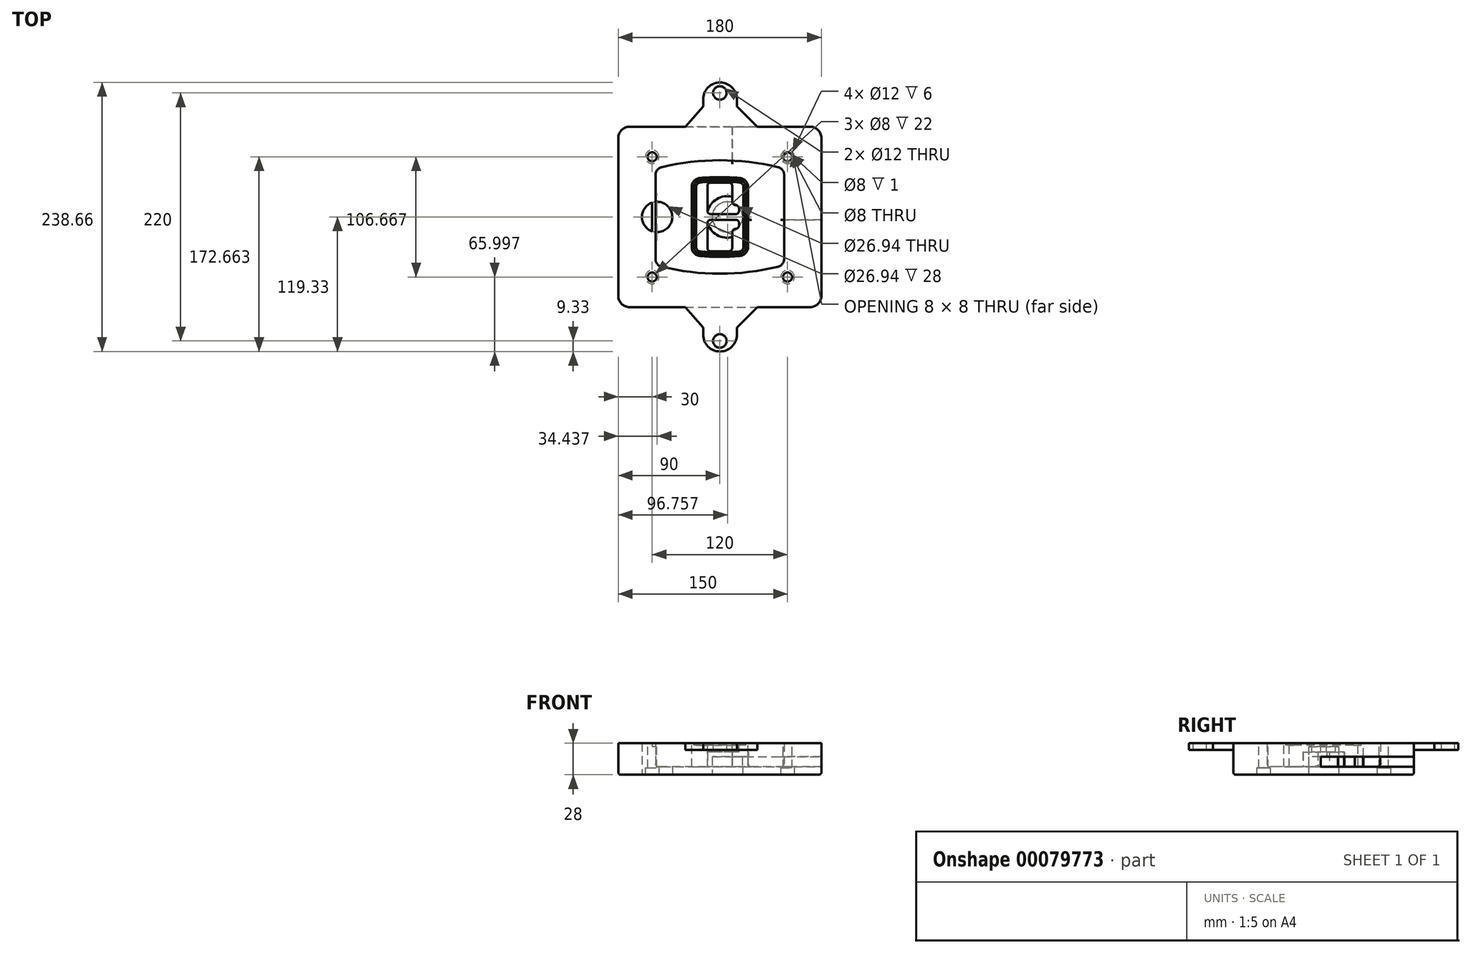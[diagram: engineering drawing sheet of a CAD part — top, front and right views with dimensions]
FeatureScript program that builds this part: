
annotation { "Feature Type Name" : "Feature", "Feature Type Description" : "" }
export const myFeature = defineFeature(function(context is Context, id is Id, definition is map)
    precondition{}
    {
        {
            var Q0;
            Q0=qCreatedBy(makeId("Top.planeOp"),FACE);
            var sketch = newSketch(context, id + "F0", { "sketchPlane" : qUnion([Q0])});
            skPoint(sketch, "E0.rect.middle", {"position": v(0, 0) * mm});
            skLineSegment(sketch, "E1.bottom", {"start": v(-80, -80) * mm, "end": v(80, -80) * mm});
            skLineSegment(sketch, "E1.top", {"start": v(-80, 80) * mm, "end": v(80, 80) * mm});
            skLineSegment(sketch, "E1.left", {"start": v(-90, -70) * mm, "end": v(-90, 70) * mm});
            skLineSegment(sketch, "E1.right", {"start": v(90, -70) * mm, "end": v(90, 70) * mm});
            skLineSegment(sketch, "E2", {"start": v(-90, 80) * mm, "end": v(90, -80) * mm, "construction": true});
            skLineSegment(sketch, "E3", {"start": v(90, 80) * mm, "end": v(-90, -80) * mm, "construction": true});
            skCircle(sketch, "E4", {"center": v(-60, 53.33) * mm, "radius": 4 * mm});
            skCircle(sketch, "E5", {"center": v(60, 53.33) * mm, "radius": 4 * mm});
            skCircle(sketch, "E6", {"center": v(60, -53.33) * mm, "radius": 4 * mm});
            skCircle(sketch, "E7", {"center": v(-60, -53.33) * mm, "radius": 4 * mm});
            skLineSegment(sketch, "E8", {"start": v(-60, 53.33) * mm, "end": v(60, 53.33) * mm, "construction": true});
            skLineSegment(sketch, "E9", {"start": v(60, 53.33) * mm, "end": v(60, -53.33) * mm, "construction": true});
            skLineSegment(sketch, "E10", {"start": v(60, -53.33) * mm, "end": v(-60, -53.33) * mm, "construction": true});
            skLineSegment(sketch, "E11", {"start": v(-60, -53.33) * mm, "end": v(-60, 53.33) * mm, "construction": true});
            skLineSegment(sketch, "E12", {"start": v(-60, 37.3) * mm, "end": v(-60, -37.3) * mm});
            skLineSegment(sketch, "E13", {"start": v(60, 37.3) * mm, "end": v(60, -37.3) * mm});
            skArc(sketch, "E14", {"start": v(52.38, 47.01) * mm, "mid": v(0, 53.33) * mm, "end": v(-52.38, 47.01) * mm});
            skArc(sketch, "E15", {"start": v(-52.38, -47.01) * mm, "mid": v(0, -53.33) * mm, "end": v(52.38, -47.01) * mm});
            skLineSegment(sketch, "E16", {"start": v(-60, 0) * mm, "end": v(60, 0) * mm, "construction": true});
            skPoint(sketch, "E17.visualSharp", {"position": v(-60, -45) * mm});
            skArc(sketch, "E17.filletArc", {"start": v(-60, -37.3) * mm, "mid": v(-57.87, -43.47) * mm, "end": v(-52.38, -47.01) * mm});
            skPoint(sketch, "E18.visualSharp", {"position": v(-60, 45) * mm});
            skArc(sketch, "E18.filletArc", {"start": v(-52.38, 47.01) * mm, "mid": v(-57.87, 43.47) * mm, "end": v(-60, 37.3) * mm});
            skPoint(sketch, "E19.visualSharp", {"position": v(60, 45) * mm});
            skArc(sketch, "E19.filletArc", {"start": v(60, 37.3) * mm, "mid": v(57.87, 43.47) * mm, "end": v(52.38, 47.01) * mm});
            skPoint(sketch, "E20.visualSharp", {"position": v(60, -45) * mm});
            skArc(sketch, "E20.filletArc", {"start": v(52.38, -47.01) * mm, "mid": v(57.87, -43.47) * mm, "end": v(60, -37.3) * mm});
            skPoint(sketch, "E21.visualSharp", {"position": v(-90, 80) * mm});
            skArc(sketch, "E21.filletArc", {"start": v(-80, 80) * mm, "mid": v(-87.07, 77.07) * mm, "end": v(-90, 70) * mm});
            skPoint(sketch, "E22.visualSharp", {"position": v(90, 80) * mm});
            skArc(sketch, "E22.filletArc", {"start": v(90, 70) * mm, "mid": v(87.07, 77.07) * mm, "end": v(80, 80) * mm});
            skPoint(sketch, "E23.visualSharp", {"position": v(90, -80) * mm});
            skArc(sketch, "E23.filletArc", {"start": v(80, -80) * mm, "mid": v(87.07, -77.07) * mm, "end": v(90, -70) * mm});
            skPoint(sketch, "E24.visualSharp", {"position": v(-90, -80) * mm});
            skArc(sketch, "E24.filletArc", {"start": v(-90, -70) * mm, "mid": v(-87.07, -77.07) * mm, "end": v(-80, -80) * mm});
            skArc(sketch, "E25.0", {"start": v(57, 37.3) * mm, "mid": v(55.5, 41.62) * mm, "end": v(51.67, 44.1) * mm});
            skLineSegment(sketch, "E25.1", {"start": v(57, 37.3) * mm, "end": v(57, -37.3) * mm});
            skArc(sketch, "E25.2", {"start": v(51.67, -44.1) * mm, "mid": v(55.5, -41.62) * mm, "end": v(57, -37.3) * mm});
            skArc(sketch, "E25.3", {"start": v(-51.67, -44.1) * mm, "mid": v(0, -50.33) * mm, "end": v(51.67, -44.1) * mm});
            skArc(sketch, "E25.4", {"start": v(-57, -37.3) * mm, "mid": v(-55.5, -41.62) * mm, "end": v(-51.67, -44.1) * mm});
            skArc(sketch, "E25.5", {"start": v(51.67, 44.1) * mm, "mid": v(0, 50.33) * mm, "end": v(-51.67, 44.1) * mm});
            skLineSegment(sketch, "E25.6", {"start": v(-57, 37.3) * mm, "end": v(-57, -37.3) * mm});
            skArc(sketch, "E25.7", {"start": v(-51.67, 44.1) * mm, "mid": v(-55.5, 41.62) * mm, "end": v(-57, 37.3) * mm});
            skArc(sketch, "E26.0", {"start": v(-53.33, 50.9) * mm, "mid": v(-61.01, 45.94) * mm, "end": v(-64, 37.3) * mm});
            skArc(sketch, "E26.1", {"start": v(53.33, 50.9) * mm, "mid": v(0, 57.33) * mm, "end": v(-53.33, 50.9) * mm});
            skArc(sketch, "E26.2", {"start": v(64, 37.3) * mm, "mid": v(61.01, 45.94) * mm, "end": v(53.33, 50.9) * mm});
            skLineSegment(sketch, "E26.3", {"start": v(64, 37.3) * mm, "end": v(64, -37.3) * mm});
            skArc(sketch, "E26.4", {"start": v(53.33, -50.9) * mm, "mid": v(61.01, -45.94) * mm, "end": v(64, -37.3) * mm});
            skLineSegment(sketch, "E26.5", {"start": v(-64, 37.3) * mm, "end": v(-64, -37.3) * mm});
            skArc(sketch, "E26.6", {"start": v(-53.33, -50.9) * mm, "mid": v(0, -57.33) * mm, "end": v(53.33, -50.9) * mm});
            skArc(sketch, "E26.7", {"start": v(-64, -37.3) * mm, "mid": v(-61.01, -45.94) * mm, "end": v(-53.33, -50.9) * mm});
            skSolve(sketch);
        }
        {
            var Q0;
            Q0=makeQuery(id+"F0.imprint","IMPRINT",FACE,{"disambiguationData":[TD([[makeQuery(id+"F0.imprint","IMPRINT",EDGE,{"derivedFrom":sQuery(id+"F0.wireOp",EDGE,"E1.bottom")}),1.0]])]});
            var Q1;
            Q1=makeQuery(id+"F0.imprint","IMPRINT",FACE,{"disambiguationData":[TD([[makeQuery(id+"F0.imprint","IMPRINT",EDGE,{"derivedFrom":sQuery(id+"F0.wireOp",EDGE,"E12")}),1.0]])]});
            var Q2;
            Q2=makeQuery(id+"F0.imprint","IMPRINT",FACE,{"disambiguationData":[TD([[makeQuery(id+"F0.imprint","IMPRINT",EDGE,{"derivedFrom":sQuery(id+"F0.wireOp",EDGE,"E25.0")}),1.0]])]});
            var Q3;
            Q3=makeQuery(id+"F0.imprint","IMPRINT",FACE,{"disambiguationData":[TD([[makeQuery(id+"F0.imprint","IMPRINT",EDGE,{"derivedFrom":sQuery(id+"F0.wireOp",EDGE,"E12")}),-1.0]])]});
            extrude(context, id + "F1", {"entities" : qUnion([Q0, Q1, Q2, Q3]), "oppositeDirection" : true, "depth" : 25 * mm});
        }
        {
            var Q0;
            Q0=makeQuery(id+"F0.imprint","IMPRINT",FACE,{"disambiguationData":[TD([[makeQuery(id+"F0.imprint","IMPRINT",EDGE,{"derivedFrom":sQuery(id+"F0.wireOp",EDGE,"E12")}),1.0]])]});
            extrude(context, id + "F2", {"entities" : qUnion([Q0]), "operationType" : NewBodyOperationType.ADD, "depth" : 3 * mm});
        }
        {
            var Q0;
            Q0=makeQuery(id+"F0.imprint","IMPRINT",FACE,{"disambiguationData":[TD([[makeQuery(id+"F0.imprint","IMPRINT",EDGE,{"derivedFrom":sQuery(id+"F0.wireOp",EDGE,"E25.0")}),1.0]])]});
            extrude(context, id + "F3", {"entities" : qUnion([Q0]), "operationType" : NewBodyOperationType.REMOVE, "oppositeDirection" : true, "depth" : 18 * mm});
        }
        {
            var Q0;
            Q0=makeQuery(id+"F2.opExtrude","CAP_FACE",FACE,{"disambiguationData":[OSD([sQuery(id+"F0.wireOp",EDGE,"E12"),sQuery(id+"F0.wireOp",EDGE,"E13"),sQuery(id+"F0.wireOp",EDGE,"E14"),sQuery(id+"F0.wireOp",EDGE,"E15"),sQuery(id+"F0.wireOp",EDGE,"E17.filletArc"),sQuery(id+"F0.wireOp",EDGE,"E18.filletArc"),sQuery(id+"F0.wireOp",EDGE,"E19.filletArc"),sQuery(id+"F0.wireOp",EDGE,"E20.filletArc"),sQuery(id+"F0.wireOp",EDGE,"E25.0"),sQuery(id+"F0.wireOp",EDGE,"E25.1"),sQuery(id+"F0.wireOp",EDGE,"E25.2"),sQuery(id+"F0.wireOp",EDGE,"E25.3"),sQuery(id+"F0.wireOp",EDGE,"E25.4"),sQuery(id+"F0.wireOp",EDGE,"E25.5"),sQuery(id+"F0.wireOp",EDGE,"E25.6"),sQuery(id+"F0.wireOp",EDGE,"E25.7")])],"isStart":false});
            var sketch = newSketch(context, id + "F4", { "sketchPlane" : qUnion([Q0])});
            skArc(sketch, "E27.0", {"start": v(-17.7, -34.56) * mm, "mid": v(0, -35.33) * mm, "end": v(17.7, -34.56) * mm});
            skArc(sketch, "E28.0", {"start": v(17.7, 34.56) * mm, "mid": v(0, 35.33) * mm, "end": v(-17.7, 34.56) * mm});
            skLineSegment(sketch, "E29", {"start": v(-25, 26.59) * mm, "end": v(-25, -26.59) * mm});
            skLineSegment(sketch, "E30", {"start": v(25, 26.59) * mm, "end": v(25, -26.59) * mm});
            skLineSegment(sketch, "E31", {"start": v(-25, 33.78) * mm, "end": v(25, 33.78) * mm, "construction": true});
            skLineSegment(sketch, "E32", {"start": v(-25, -33.78) * mm, "end": v(25, -33.78) * mm, "construction": true});
            skPoint(sketch, "E33.visualSharp", {"position": v(-25, 33.78) * mm});
            skArc(sketch, "E33.filletArc", {"start": v(-17.7, 34.56) * mm, "mid": v(-22.9, 32) * mm, "end": v(-25, 26.59) * mm});
            skPoint(sketch, "E34.visualSharp", {"position": v(25, 33.78) * mm});
            skArc(sketch, "E34.filletArc", {"start": v(25, 26.59) * mm, "mid": v(22.9, 32) * mm, "end": v(17.7, 34.56) * mm});
            skPoint(sketch, "E35.visualSharp", {"position": v(25, -33.78) * mm});
            skArc(sketch, "E35.filletArc", {"start": v(17.7, -34.56) * mm, "mid": v(22.9, -32) * mm, "end": v(25, -26.59) * mm});
            skPoint(sketch, "E36.visualSharp", {"position": v(-25, -33.78) * mm});
            skArc(sketch, "E36.filletArc", {"start": v(-25, -26.59) * mm, "mid": v(-22.9, -32) * mm, "end": v(-17.7, -34.56) * mm});
            skArc(sketch, "E37.0", {"start": v(51.67, 44.1) * mm, "mid": v(0, 50.33) * mm, "end": v(-51.67, 44.1) * mm});
            skArc(sketch, "E37.1", {"start": v(-51.67, 44.1) * mm, "mid": v(-55.5, 41.62) * mm, "end": v(-57, 37.3) * mm});
            skLineSegment(sketch, "E37.2", {"start": v(-57, 37.3) * mm, "end": v(-57, -37.3) * mm});
            skArc(sketch, "E37.3", {"start": v(-57, -37.3) * mm, "mid": v(-55.5, -41.62) * mm, "end": v(-51.67, -44.1) * mm});
            skArc(sketch, "E37.4", {"start": v(-51.67, -44.1) * mm, "mid": v(0, -50.33) * mm, "end": v(51.67, -44.1) * mm});
            skArc(sketch, "E37.5", {"start": v(51.67, -44.1) * mm, "mid": v(55.5, -41.62) * mm, "end": v(57, -37.3) * mm});
            skLineSegment(sketch, "E37.6", {"start": v(57, 37.3) * mm, "end": v(57, -37.3) * mm});
            skArc(sketch, "E37.7", {"start": v(57, 37.3) * mm, "mid": v(55.5, 41.62) * mm, "end": v(51.67, 44.1) * mm});
            skLineSegment(sketch, "E38.0", {"start": v(23, 26.59) * mm, "end": v(23, -26.59) * mm});
            skArc(sketch, "E38.1", {"start": v(17.53, -32.56) * mm, "mid": v(21.42, -30.64) * mm, "end": v(23, -26.59) * mm});
            skArc(sketch, "E38.2", {"start": v(-17.53, -32.56) * mm, "mid": v(0, -33.33) * mm, "end": v(17.53, -32.56) * mm});
            skArc(sketch, "E38.3", {"start": v(-23, -26.59) * mm, "mid": v(-21.42, -30.64) * mm, "end": v(-17.53, -32.56) * mm});
            skLineSegment(sketch, "E38.4", {"start": v(-23, 26.59) * mm, "end": v(-23, -26.59) * mm});
            skArc(sketch, "E38.5", {"start": v(23, 26.59) * mm, "mid": v(21.42, 30.64) * mm, "end": v(17.53, 32.56) * mm});
            skArc(sketch, "E38.6", {"start": v(-17.53, 32.56) * mm, "mid": v(-21.42, 30.64) * mm, "end": v(-23, 26.59) * mm});
            skArc(sketch, "E38.7", {"start": v(17.53, 32.56) * mm, "mid": v(0, 33.33) * mm, "end": v(-17.53, 32.56) * mm});
            skArc(sketch, "E39.0", {"start": v(21, 26.59) * mm, "mid": v(19.95, 29.29) * mm, "end": v(17.35, 30.57) * mm});
            skLineSegment(sketch, "E39.1", {"start": v(21, 26.59) * mm, "end": v(21, -26.59) * mm});
            skArc(sketch, "E39.2", {"start": v(17.35, -30.57) * mm, "mid": v(19.95, -29.29) * mm, "end": v(21, -26.59) * mm});
            skArc(sketch, "E39.3", {"start": v(-17.35, -30.57) * mm, "mid": v(0, -31.33) * mm, "end": v(17.35, -30.57) * mm});
            skArc(sketch, "E39.4", {"start": v(-21, -26.59) * mm, "mid": v(-19.95, -29.29) * mm, "end": v(-17.35, -30.57) * mm});
            skArc(sketch, "E39.5", {"start": v(17.35, 30.57) * mm, "mid": v(0, 31.33) * mm, "end": v(-17.35, 30.57) * mm});
            skLineSegment(sketch, "E39.6", {"start": v(-21, 26.59) * mm, "end": v(-21, -26.59) * mm});
            skArc(sketch, "E39.7", {"start": v(-17.35, 30.57) * mm, "mid": v(-19.95, 29.29) * mm, "end": v(-21, 26.59) * mm});
            skLineSegment(sketch, "E40", {"start": v(-25, 0) * mm, "end": v(25, 0) * mm, "construction": true});
            skLineSegment(sketch, "E41", {"start": v(-11, 5.5) * mm, "end": v(-11, 27.5) * mm});
            skLineSegment(sketch, "E42", {"start": v(-8, 30.5) * mm, "end": v(8, 30.5) * mm});
            skLineSegment(sketch, "E43", {"start": v(11, 27.5) * mm, "end": v(11, 13.5) * mm});
            skLineSegment(sketch, "E44", {"start": v(14, 10.5) * mm, "end": v(14, 10.5) * mm});
            skLineSegment(sketch, "E45", {"start": v(17, 7.5) * mm, "end": v(17, 5.5) * mm});
            skLineSegment(sketch, "E46", {"start": v(14, 2.5) * mm, "end": v(-8, 2.5) * mm});
            skPoint(sketch, "E47.visualSharp", {"position": v(-11, 30.5) * mm});
            skArc(sketch, "E47.filletArc", {"start": v(-8, 30.5) * mm, "mid": v(-10.12, 29.62) * mm, "end": v(-11, 27.5) * mm});
            skPoint(sketch, "E48.visualSharp", {"position": v(11, 30.5) * mm});
            skArc(sketch, "E48.filletArc", {"start": v(11, 27.5) * mm, "mid": v(10.12, 29.62) * mm, "end": v(8, 30.5) * mm});
            skPoint(sketch, "E49.visualSharp", {"position": v(11, 10.5) * mm});
            skArc(sketch, "E49.filletArc", {"start": v(11, 13.5) * mm, "mid": v(11.88, 11.38) * mm, "end": v(14, 10.5) * mm});
            skPoint(sketch, "E50.visualSharp", {"position": v(17, 10.5) * mm});
            skArc(sketch, "E50.filletArc", {"start": v(17, 7.5) * mm, "mid": v(16.12, 9.62) * mm, "end": v(14, 10.5) * mm});
            skPoint(sketch, "E51.visualSharp", {"position": v(17, 2.5) * mm});
            skArc(sketch, "E51.filletArc", {"start": v(14, 2.5) * mm, "mid": v(16.12, 3.38) * mm, "end": v(17, 5.5) * mm});
            skPoint(sketch, "E52.visualSharp", {"position": v(-11, 2.5) * mm});
            skArc(sketch, "E52.filletArc", {"start": v(-11, 5.5) * mm, "mid": v(-10.12, 3.38) * mm, "end": v(-8, 2.5) * mm});
            skLineSegment(sketch, "E53.0.MirrorCS", {"start": v(14, -2.5) * mm, "end": v(-8, -2.5) * mm});
            skArc(sketch, "E54.0.MirrorCS", {"start": v(-11, -5.5) * mm, "mid": v(-10.12, -3.38) * mm, "end": v(-8, -2.5) * mm});
            skLineSegment(sketch, "E55.0.MirrorCS", {"start": v(-11, -5.5) * mm, "end": v(-11, -27.5) * mm});
            skArc(sketch, "E56.0.MirrorCS", {"start": v(-8, -30.5) * mm, "mid": v(-10.12, -29.62) * mm, "end": v(-11, -27.5) * mm});
            skLineSegment(sketch, "E57.0.MirrorCS", {"start": v(-8, -30.5) * mm, "end": v(8, -30.5) * mm});
            skArc(sketch, "E58.0.MirrorCS", {"start": v(11, -27.5) * mm, "mid": v(10.12, -29.62) * mm, "end": v(8, -30.5) * mm});
            skLineSegment(sketch, "E59.0.MirrorCS", {"start": v(11, -27.5) * mm, "end": v(11, -13.5) * mm});
            skArc(sketch, "E60.0.MirrorCS", {"start": v(11, -13.5) * mm, "mid": v(11.88, -11.38) * mm, "end": v(14, -10.5) * mm});
            skArc(sketch, "E61.0.MirrorCS", {"start": v(17, -7.5) * mm, "mid": v(16.12, -9.62) * mm, "end": v(14, -10.5) * mm});
            skLineSegment(sketch, "E62.0.MirrorCS", {"start": v(17, -7.5) * mm, "end": v(17, -5.5) * mm});
            skArc(sketch, "E63.0.MirrorCS", {"start": v(14, -2.5) * mm, "mid": v(16.12, -3.38) * mm, "end": v(17, -5.5) * mm});
            skSolve(sketch);
        }
        {
            var Q0;
            Q0=makeQuery(id+"F4.imprint","IMPRINT",FACE,{"disambiguationData":[TD([[makeQuery(id+"F4.imprint","IMPRINT",EDGE,{"derivedFrom":sQuery(id+"F4.wireOp",EDGE,"E27.0")}),1.0]])]});
            var Q1;
            Q1=makeQuery(id+"F4.imprint","IMPRINT",FACE,{"disambiguationData":[TD([[makeQuery(id+"F4.imprint","IMPRINT",EDGE,{"derivedFrom":sQuery(id+"F4.wireOp",EDGE,"E38.0")}),-1.0]])]});
            var Q2;
            Q2=makeQuery(id+"F4.imprint","IMPRINT",FACE,{"disambiguationData":[TD([[makeQuery(id+"F4.imprint","IMPRINT",EDGE,{"derivedFrom":sQuery(id+"F4.wireOp",EDGE,"E39.0")}),1.0]])]});
            extrude(context, id + "F5", {"entities" : qUnion([Q0, Q1, Q2]), "operationType" : NewBodyOperationType.ADD, "endBound" : BoundingType.UP_TO_NEXT, "oppositeDirection" : true, "depth" : 25 * mm});
        }
        {
            var Q0;
            Q0=makeQuery(id+"F4.imprint","IMPRINT",FACE,{"disambiguationData":[TD([[makeQuery(id+"F4.imprint","IMPRINT",EDGE,{"derivedFrom":sQuery(id+"F4.wireOp",EDGE,"E38.0")}),-1.0]])]});
            extrude(context, id + "F6", {"entities" : qUnion([Q0]), "operationType" : NewBodyOperationType.REMOVE, "oppositeDirection" : true, "depth" : 2 * mm});
        }
        {
            var Q0;
            Q0=makeQuery(id+"F1.opExtrude","CAP_FACE",FACE,{"disambiguationData":[OSD([sQuery(id+"F0.wireOp",EDGE,"E1.bottom"),sQuery(id+"F0.wireOp",EDGE,"E1.top"),sQuery(id+"F0.wireOp",EDGE,"E1.left"),sQuery(id+"F0.wireOp",EDGE,"E1.right"),sQuery(id+"F0.wireOp",EDGE,"E4"),sQuery(id+"F0.wireOp",EDGE,"E5"),sQuery(id+"F0.wireOp",EDGE,"E6"),sQuery(id+"F0.wireOp",EDGE,"E7"),sQuery(id+"F0.wireOp",EDGE,"E21.filletArc"),sQuery(id+"F0.wireOp",EDGE,"E22.filletArc"),sQuery(id+"F0.wireOp",EDGE,"E23.filletArc"),sQuery(id+"F0.wireOp",EDGE,"E24.filletArc")])],"isStart":false});
            var sketch = newSketch(context, id + "F7", { "sketchPlane" : qUnion([Q0])});
            skCircle(sketch, "E64", {"center": v(6.76, 0) * mm, "radius": 13.47 * mm});
            skCircle(sketch, "E65", {"center": v(-55.56, 0) * mm, "radius": 13.47 * mm});
            skLineSegment(sketch, "E66", {"start": v(90, 0) * mm, "end": v(-90, 0) * mm});
            skCircle(sketch, "E67", {"center": v(6.76, 0) * mm, "radius": 18.47 * mm});
            skCircle(sketch, "E68", {"center": v(60, -53.33) * mm, "radius": 6 * mm});
            skCircle(sketch, "E69", {"center": v(-60, -53.33) * mm, "radius": 6 * mm});
            skCircle(sketch, "E70", {"center": v(-60, 53.33) * mm, "radius": 6 * mm});
            skCircle(sketch, "E71", {"center": v(60, 53.33) * mm, "radius": 6 * mm});
            skSolve(sketch);
        }
        {
            var Q0;
            {var subQ1=sQuery(id+"F7.wireOp",EDGE,"E66");var subQ4=sQuery(id+"F7.wireOp",EDGE,"E64");var subQ6=makeQuery(id+"F7.imprint","INTERSECT",VERTEX,{"disambiguationData":[OD(0.0)],"derivedFrom":[subQ4,subQ1]});Q0=makeQuery(id+"F7.imprint","IMPRINT",FACE,{"disambiguationData":[TD([[makeQuery(id+"F7.imprint","IMPRINT",EDGE,{"disambiguationData":[TD([[subQ6,-1.0]])],"derivedFrom":subQ4}),-1.0]])]});}
            var Q1;
            {var subQ0=sQuery(id+"F7.wireOp",EDGE,"E66");var subQ1=sQuery(id+"F7.wireOp",EDGE,"E64");var subQ3=makeQuery(id+"F7.imprint","INTERSECT",VERTEX,{"disambiguationData":[OD(0.0)],"derivedFrom":[subQ1,subQ0]});Q1=makeQuery(id+"F7.imprint","IMPRINT",FACE,{"disambiguationData":[TD([[makeQuery(id+"F7.imprint","IMPRINT",EDGE,{"disambiguationData":[TD([[subQ3,-1.0]])],"derivedFrom":subQ1}),1.0]])]});}
            var Q2;
            {var subQ0=sQuery(id+"F7.wireOp",EDGE,"E66");var subQ1=sQuery(id+"F7.wireOp",EDGE,"E64");var subQ3=makeQuery(id+"F7.imprint","INTERSECT",VERTEX,{"disambiguationData":[OD(0.0)],"derivedFrom":[subQ1,subQ0]});Q2=makeQuery(id+"F7.imprint","IMPRINT",FACE,{"disambiguationData":[TD([[makeQuery(id+"F7.imprint","IMPRINT",EDGE,{"disambiguationData":[TD([[subQ3,1.0]])],"derivedFrom":subQ1}),1.0]])]});}
            var Q3;
            {var subQ1=sQuery(id+"F7.wireOp",EDGE,"E66");var subQ4=sQuery(id+"F7.wireOp",EDGE,"E64");var subQ6=makeQuery(id+"F7.imprint","INTERSECT",VERTEX,{"disambiguationData":[OD(0.0)],"derivedFrom":[subQ4,subQ1]});Q3=makeQuery(id+"F7.imprint","IMPRINT",FACE,{"disambiguationData":[TD([[makeQuery(id+"F7.imprint","IMPRINT",EDGE,{"disambiguationData":[TD([[subQ6,1.0]])],"derivedFrom":subQ4}),-1.0]])]});}
            extrude(context, id + "F8", {"entities" : qUnion([Q0, Q1, Q2, Q3]), "operationType" : NewBodyOperationType.ADD, "oppositeDirection" : true, "depth" : 20 * mm});
        }
        {
            var Q0;
            {var subQ0=sQuery(id+"F7.wireOp",EDGE,"E66");var subQ1=sQuery(id+"F7.wireOp",EDGE,"E64");var subQ3=makeQuery(id+"F7.imprint","INTERSECT",VERTEX,{"disambiguationData":[OD(0.0)],"derivedFrom":[subQ1,subQ0]});Q0=makeQuery(id+"F7.imprint","IMPRINT",FACE,{"disambiguationData":[TD([[makeQuery(id+"F7.imprint","IMPRINT",EDGE,{"disambiguationData":[TD([[subQ3,-1.0]])],"derivedFrom":subQ1}),1.0]])]});}
            var Q1;
            {var subQ0=sQuery(id+"F7.wireOp",EDGE,"E66");var subQ1=sQuery(id+"F7.wireOp",EDGE,"E64");var subQ3=makeQuery(id+"F7.imprint","INTERSECT",VERTEX,{"disambiguationData":[OD(0.0)],"derivedFrom":[subQ1,subQ0]});Q1=makeQuery(id+"F7.imprint","IMPRINT",FACE,{"disambiguationData":[TD([[makeQuery(id+"F7.imprint","IMPRINT",EDGE,{"disambiguationData":[TD([[subQ3,1.0]])],"derivedFrom":subQ1}),1.0]])]});}
            extrude(context, id + "F9", {"entities" : qUnion([Q0, Q1]), "operationType" : NewBodyOperationType.REMOVE, "oppositeDirection" : true, "depth" : 16 * mm});
        }
        {
            var Q0;
            {var subQ0=sQuery(id+"F7.wireOp",EDGE,"E66");var subQ1=sQuery(id+"F7.wireOp",EDGE,"E65");var subQ3=makeQuery(id+"F7.imprint","INTERSECT",VERTEX,{"disambiguationData":[OD(0.0)],"derivedFrom":[subQ1,subQ0]});Q0=makeQuery(id+"F7.imprint","IMPRINT",FACE,{"disambiguationData":[TD([[makeQuery(id+"F7.imprint","IMPRINT",EDGE,{"disambiguationData":[TD([[subQ3,-1.0]])],"derivedFrom":subQ1}),1.0]])]});}
            var Q1;
            {var subQ0=sQuery(id+"F7.wireOp",EDGE,"E66");var subQ1=sQuery(id+"F7.wireOp",EDGE,"E65");var subQ3=makeQuery(id+"F7.imprint","INTERSECT",VERTEX,{"disambiguationData":[OD(0.0)],"derivedFrom":[subQ1,subQ0]});Q1=makeQuery(id+"F7.imprint","IMPRINT",FACE,{"disambiguationData":[TD([[makeQuery(id+"F7.imprint","IMPRINT",EDGE,{"disambiguationData":[TD([[subQ3,1.0]])],"derivedFrom":subQ1}),1.0]])]});}
            extrude(context, id + "F10", {"entities" : qUnion([Q0, Q1]), "operationType" : NewBodyOperationType.REMOVE, "oppositeDirection" : true, "depth" : 25 * mm});
        }
        {
            var Q0;
            Q0=makeQuery(id+"F7.imprint","IMPRINT",FACE,{"disambiguationData":[TD([[makeQuery(id+"F7.imprint","IMPRINT",EDGE,{"derivedFrom":sQuery(id+"F7.wireOp",EDGE,"E68")}),1.0]])]});
            var Q1;
            Q1=makeQuery(id+"F7.imprint","IMPRINT",FACE,{"disambiguationData":[TD([[makeQuery(id+"F7.imprint","IMPRINT",EDGE,{"derivedFrom":makeQuery(id+"F1.opExtrude","CAP_EDGE",EDGE,{"disambiguationData":[OSD([sQuery(id+"F0.wireOp",EDGE,"E5")])],"isStart":false})}),-1.0]])]});
            var Q2;
            Q2=makeQuery(id+"F7.imprint","IMPRINT",FACE,{"disambiguationData":[TD([[makeQuery(id+"F7.imprint","IMPRINT",EDGE,{"derivedFrom":sQuery(id+"F7.wireOp",EDGE,"E69")}),1.0]])]});
            var Q3;
            Q3=makeQuery(id+"F7.imprint","IMPRINT",FACE,{"disambiguationData":[TD([[makeQuery(id+"F7.imprint","IMPRINT",EDGE,{"derivedFrom":makeQuery(id+"F1.opExtrude","CAP_EDGE",EDGE,{"disambiguationData":[OSD([sQuery(id+"F0.wireOp",EDGE,"E4")])],"isStart":false})}),-1.0]])]});
            var Q4;
            Q4=makeQuery(id+"F7.imprint","IMPRINT",FACE,{"disambiguationData":[TD([[makeQuery(id+"F7.imprint","IMPRINT",EDGE,{"derivedFrom":sQuery(id+"F7.wireOp",EDGE,"E70")}),1.0]])]});
            var Q5;
            Q5=makeQuery(id+"F7.imprint","IMPRINT",FACE,{"disambiguationData":[TD([[makeQuery(id+"F7.imprint","IMPRINT",EDGE,{"derivedFrom":makeQuery(id+"F1.opExtrude","CAP_EDGE",EDGE,{"disambiguationData":[OSD([sQuery(id+"F0.wireOp",EDGE,"E7")])],"isStart":false})}),-1.0]])]});
            var Q6;
            Q6=makeQuery(id+"F7.imprint","IMPRINT",FACE,{"disambiguationData":[TD([[makeQuery(id+"F7.imprint","IMPRINT",EDGE,{"derivedFrom":sQuery(id+"F7.wireOp",EDGE,"E71")}),1.0]])]});
            var Q7;
            Q7=makeQuery(id+"F7.imprint","IMPRINT",FACE,{"disambiguationData":[TD([[makeQuery(id+"F7.imprint","IMPRINT",EDGE,{"derivedFrom":makeQuery(id+"F1.opExtrude","CAP_EDGE",EDGE,{"disambiguationData":[OSD([sQuery(id+"F0.wireOp",EDGE,"E6")])],"isStart":false})}),-1.0]])]});
            extrude(context, id + "F11", {"entities" : qUnion([Q0, Q1, Q2, Q3, Q4, Q5, Q6, Q7]), "operationType" : NewBodyOperationType.REMOVE, "oppositeDirection" : true, "depth" : 6 * mm});
        }
        {
            var Q0;
            Q0=makeQuery(id+"F9.boolean.opBoolean","COPY",FACE,{"derivedFrom":makeQuery(id+"F9.opExtrude","CAP_FACE",FACE,{"disambiguationData":[OSD([sQuery(id+"F7.wireOp",EDGE,"E64")])],"isStart":false})});
            var sketch = newSketch(context, id + "F12", { "sketchPlane" : qUnion([Q0])});
            skArc(sketch, "E72.0", {"start": v(11, -88.19) * mm, "mid": v(97.1, -83.6) * mm, "end": v(92.5, 2.5) * mm});
            skLineSegment(sketch, "E72.1", {"start": v(11, -17.97) * mm, "end": v(11, -17.97) * mm});
            skLineSegment(sketch, "E73", {"start": v(92.5, -105.13) * mm, "end": v(102.3, -105.13) * mm});
            skLineSegment(sketch, "E74.0", {"start": v(92.5, 2.5) * mm, "end": v(14, 2.5) * mm});
            skArc(sketch, "E74.1", {"start": v(14, 2.5) * mm, "mid": v(16.12, 3.38) * mm, "end": v(17, 5.5) * mm});
            skLineSegment(sketch, "E74.2", {"start": v(17, 7.5) * mm, "end": v(17, 5.5) * mm});
            skArc(sketch, "E74.3", {"start": v(17, 7.5) * mm, "mid": v(16.12, 9.62) * mm, "end": v(14, 10.5) * mm});
            skArc(sketch, "E74.4", {"start": v(11, 13.5) * mm, "mid": v(11.88, 11.38) * mm, "end": v(14, 10.5) * mm});
            skLineSegment(sketch, "E74.5", {"start": v(11, 13.5) * mm, "end": v(11, -88.19) * mm});
            skLineSegment(sketch, "E74.7", {"start": v(92.5, -2.5) * mm, "end": v(14, -2.5) * mm});
            skArc(sketch, "E74.8", {"start": v(14, -2.5) * mm, "mid": v(16.12, -3.38) * mm, "end": v(17, -5.5) * mm});
            skLineSegment(sketch, "E74.9", {"start": v(17, -7.5) * mm, "end": v(17, -5.5) * mm});
            skArc(sketch, "E74.10", {"start": v(17, -7.5) * mm, "mid": v(16.12, -9.62) * mm, "end": v(14, -10.5) * mm});
            skArc(sketch, "E74.11", {"start": v(11, -13.5) * mm, "mid": v(11.88, -11.38) * mm, "end": v(14, -10.5) * mm});
            skLineSegment(sketch, "E74.12", {"start": v(11, -17.97) * mm, "end": v(11, -13.5) * mm});
            skPoint(sketch, "E75.orphan", {"position": v(11, -27.5) * mm});
            skPoint(sketch, "E76.orphan", {"position": v(-8, -2.5) * mm});
            skPoint(sketch, "E77.orphan", {"position": v(-8, 2.5) * mm});
            skPoint(sketch, "E78.orphan", {"position": v(11, 27.5) * mm});
            skSolve(sketch);
        }
        {
            var Q0;
            {var subQ7=sQuery(id+"F12.wireOp",EDGE,"E72.0");var subQ14=sQuery(id+"F12.wireOp",EDGE,"E72.1");var subQ16=sQuery(id+"F12.wireOp",EDGE,"E74.1");var subQ18=sQuery(id+"F12.wireOp",EDGE,"E74.8");Q0=qUnion([makeQuery(id+"F12.imprint","IMPRINT",FACE,{"disambiguationData":[TD([[makeQuery(id+"F12.imprint","IMPRINT",EDGE,{"derivedFrom":subQ7}),1.0]])]}),makeQuery(id+"F12.imprint","IMPRINT",FACE,{"disambiguationData":[TD([[makeQuery(id+"F12.imprint","IMPRINT",EDGE,{"derivedFrom":subQ14}),1.0]])]}),makeQuery(id+"F12.imprint","IMPRINT",FACE,{"disambiguationData":[TD([[makeQuery(id+"F12.imprint","IMPRINT",EDGE,{"derivedFrom":subQ16}),1.0]])]}),makeQuery(id+"F12.imprint","IMPRINT",FACE,{"disambiguationData":[TD([[makeQuery(id+"F12.imprint","IMPRINT",EDGE,{"derivedFrom":subQ18}),-1.0]])]})]);}
            var Q1;
            Q1=makeQuery(id+"F5.boolean.opBoolean","SPLIT",FACE,{"disambiguationData":[TD([makeQuery(id+"F5.opExtrude","SWEPT_FACE",FACE,{"disambiguationData":[OSD([sQuery(id+"F4.wireOp",EDGE,"E41")])]})])],"derivedFrom":makeQuery(id+"F3.boolean.opBoolean","COPY",FACE,{"derivedFrom":makeQuery(id+"F3.opExtrude","CAP_FACE",FACE,{"disambiguationData":[OSD([sQuery(id+"F0.wireOp",EDGE,"E25.0"),sQuery(id+"F0.wireOp",EDGE,"E25.1"),sQuery(id+"F0.wireOp",EDGE,"E25.2"),sQuery(id+"F0.wireOp",EDGE,"E25.3"),sQuery(id+"F0.wireOp",EDGE,"E25.4"),sQuery(id+"F0.wireOp",EDGE,"E25.5"),sQuery(id+"F0.wireOp",EDGE,"E25.6"),sQuery(id+"F0.wireOp",EDGE,"E25.7")])],"isStart":false})})});
            extrude(context, id + "F13", {"entities" : qUnion([Q0]), "operationType" : NewBodyOperationType.REMOVE, "endBound" : BoundingType.UP_TO_SURFACE, "endBoundEntityFace" : qUnion([Q1]), "depth" : 25 * mm});
        }
        {
            var Q0;
            Q0=makeQuery(id+"F3.boolean.opBoolean","COPY",EDGE,{"derivedFrom":makeQuery(id+"F3.opExtrude","CAP_EDGE",EDGE,{"disambiguationData":[OSD([sQuery(id+"F0.wireOp",EDGE,"E25.6")])],"isStart":false})});
            var Q1;
            Q1=makeQuery(id+"F8.boolean.opBoolean","INTERSECT",EDGE,{"derivedFrom":[makeQuery(id+"F5.opExtrude","SWEPT_FACE",FACE,{"disambiguationData":[OSD([sQuery(id+"F4.wireOp",EDGE,"E30")])]}),makeQuery(id+"F8.opExtrude","CAP_FACE",FACE,{"disambiguationData":[OSD([sQuery(id+"F7.wireOp",EDGE,"E67")])],"isStart":false})]});
            var Q2;
            Q2=makeQuery(id+"F8.boolean.opBoolean","INTERSECT",EDGE,{"disambiguationData":[OD(1.0)],"derivedFrom":[makeQuery(id+"F5.opExtrude","SWEPT_FACE",FACE,{"disambiguationData":[OSD([sQuery(id+"F4.wireOp",EDGE,"E30")])]}),makeQuery(id+"F8.opExtrude","SWEPT_FACE",FACE,{"disambiguationData":[OSD([sQuery(id+"F7.wireOp",EDGE,"E67")])]})]});
            var Q3;
            {var subQ0=makeQuery(id+"F3.boolean.opBoolean","COPY",FACE,{"derivedFrom":makeQuery(id+"F3.opExtrude","CAP_FACE",FACE,{"disambiguationData":[OSD([sQuery(id+"F0.wireOp",EDGE,"E25.0"),sQuery(id+"F0.wireOp",EDGE,"E25.1"),sQuery(id+"F0.wireOp",EDGE,"E25.2"),sQuery(id+"F0.wireOp",EDGE,"E25.3"),sQuery(id+"F0.wireOp",EDGE,"E25.4"),sQuery(id+"F0.wireOp",EDGE,"E25.5"),sQuery(id+"F0.wireOp",EDGE,"E25.6"),sQuery(id+"F0.wireOp",EDGE,"E25.7")])],"isStart":false})});var subQ1=sQuery(id+"F4.wireOp",EDGE,"E30");Q3=makeQuery(id+"F8.boolean.opBoolean","SPLIT",EDGE,{"disambiguationData":[TD([makeQuery(id+"F5.opExtrude","SWEPT_FACE",FACE,{"disambiguationData":[OSD([sQuery(id+"F4.wireOp",EDGE,"E35.filletArc")])]})])],"derivedFrom":makeQuery(id+"F5.opExtrude","TWEAK_EDGE",EDGE,{"derivedFrom":[subQ0,makeQuery(id+"F4.imprint","IMPRINT",EDGE,{"derivedFrom":subQ1})]})});}
            var Q4;
            {var subQ0=sQuery(id+"F0.wireOp",EDGE,"E25.0");var subQ1=sQuery(id+"F0.wireOp",EDGE,"E25.1");var subQ2=sQuery(id+"F0.wireOp",EDGE,"E25.2");var subQ3=sQuery(id+"F0.wireOp",EDGE,"E25.3");var subQ4=sQuery(id+"F0.wireOp",EDGE,"E25.4");var subQ5=sQuery(id+"F0.wireOp",EDGE,"E25.5");var subQ6=sQuery(id+"F0.wireOp",EDGE,"E25.6");var subQ7=sQuery(id+"F0.wireOp",EDGE,"E25.7");Q4=makeQuery(id+"F8.boolean.opBoolean","INTERSECT",EDGE,{"derivedFrom":[makeQuery(id+"F5.boolean.opBoolean","SPLIT",FACE,{"disambiguationData":[TD([makeQuery(id+"F2.opExtrude","SWEPT_FACE",FACE,{"disambiguationData":[OSD([subQ0])]})])],"derivedFrom":makeQuery(id+"F3.boolean.opBoolean","COPY",FACE,{"derivedFrom":makeQuery(id+"F3.opExtrude","CAP_FACE",FACE,{"disambiguationData":[OSD([subQ0,subQ1,subQ2,subQ3,subQ4,subQ5,subQ6,subQ7])],"isStart":false})})}),makeQuery(id+"F8.opExtrude","SWEPT_FACE",FACE,{"disambiguationData":[OSD([sQuery(id+"F7.wireOp",EDGE,"E67")])]})]});}
            var Q5;
            Q5=makeQuery(id+"F8.boolean.opBoolean","INTERSECT",EDGE,{"disambiguationData":[OD(0.0)],"derivedFrom":[makeQuery(id+"F5.opExtrude","SWEPT_FACE",FACE,{"disambiguationData":[OSD([sQuery(id+"F4.wireOp",EDGE,"E30")])]}),makeQuery(id+"F8.opExtrude","SWEPT_FACE",FACE,{"disambiguationData":[OSD([sQuery(id+"F7.wireOp",EDGE,"E67")])]})]});
            fillet(context, id + "F14", {"entities" : qUnion([Q0, Q1, Q2, Q3, Q4, Q5]), "radius" : 3 * mm, "tangentPropagation" : true, "allowEdgeOverflow" : false});
        }
        {
            var Q0;
            Q0=makeQuery(id+"F1.opExtrude","CAP_EDGE",EDGE,{"disambiguationData":[OSD([sQuery(id+"F0.wireOp",EDGE,"E1.bottom")])],"isStart":false});
            fillet(context, id + "F15", {"entities" : qUnion([Q0]), "radius" : 2 * mm, "tangentPropagation" : true, "allowEdgeOverflow" : false});
        }
        {
            var Q0;
            {var subQ0=sQuery(id+"F0.wireOp",EDGE,"E22.filletArc");var subQ1=sQuery(id+"F0.wireOp",EDGE,"E7");var subQ2=sQuery(id+"F0.wireOp",EDGE,"E6");var subQ3=sQuery(id+"F0.wireOp",EDGE,"E5");var subQ4=sQuery(id+"F0.wireOp",EDGE,"E4");var subQ5=sQuery(id+"F0.wireOp",EDGE,"E1.bottom");var subQ6=sQuery(id+"F0.wireOp",EDGE,"E21.filletArc");var subQ7=sQuery(id+"F0.wireOp",EDGE,"E1.top");var subQ8=sQuery(id+"F0.wireOp",EDGE,"E1.left");var subQ9=sQuery(id+"F0.wireOp",EDGE,"E1.right");var subQ10=sQuery(id+"F0.wireOp",EDGE,"E23.filletArc");var subQ11=sQuery(id+"F0.wireOp",EDGE,"E24.filletArc");Q0=makeQuery(id+"F2.boolean.opBoolean","SPLIT",FACE,{"disambiguationData":[TD([makeQuery(id+"F1.opExtrude","SWEPT_FACE",FACE,{"disambiguationData":[OSD([subQ5])]})])],"derivedFrom":makeQuery(id+"F1.opExtrude","CAP_FACE",FACE,{"disambiguationData":[OSD([subQ5,subQ7,subQ8,subQ9,subQ4,subQ3,subQ2,subQ1,subQ6,subQ0,subQ10,subQ11])],"isStart":true})});}
            var sketch = newSketch(context, id + "F16", { "sketchPlane" : qUnion([Q0])});
            skArc(sketch, "E79.0", {"start": v(-80, 80) * mm, "mid": v(-87.07, 77.07) * mm, "end": v(-90, 70) * mm});
            skLineSegment(sketch, "E79.1", {"start": v(-90, -70) * mm, "end": v(-90, 70) * mm});
            skArc(sketch, "E79.2", {"start": v(-90, -70) * mm, "mid": v(-87.07, -77.07) * mm, "end": v(-80, -80) * mm});
            skLineSegment(sketch, "E79.3", {"start": v(-80, -80) * mm, "end": v(80, -80) * mm});
            skArc(sketch, "E79.4", {"start": v(80, -80) * mm, "mid": v(87.07, -77.07) * mm, "end": v(90, -70) * mm});
            skLineSegment(sketch, "E79.5", {"start": v(90, -70) * mm, "end": v(90, 70) * mm});
            skArc(sketch, "E79.6", {"start": v(90, 70) * mm, "mid": v(87.07, 77.07) * mm, "end": v(80, 80) * mm});
            skLineSegment(sketch, "E79.7", {"start": v(-80, 80) * mm, "end": v(80, 80) * mm});
            skCircle(sketch, "E79.8", {"center": v(-60, 53.33) * mm, "radius": 4 * mm});
            skCircle(sketch, "E79.9", {"center": v(60, 53.33) * mm, "radius": 4 * mm});
            skCircle(sketch, "E79.10", {"center": v(60, -53.33) * mm, "radius": 4 * mm});
            skCircle(sketch, "E79.11", {"center": v(-60, -53.33) * mm, "radius": 4 * mm});
            skArc(sketch, "E79.12", {"start": v(52.38, 47.01) * mm, "mid": v(0, 53.33) * mm, "end": v(-52.38, 47.01) * mm});
            skArc(sketch, "E79.13", {"start": v(-52.38, 47.01) * mm, "mid": v(-57.87, 43.47) * mm, "end": v(-60, 37.3) * mm});
            skLineSegment(sketch, "E79.14", {"start": v(-60, 37.3) * mm, "end": v(-60, -37.3) * mm});
            skArc(sketch, "E79.15", {"start": v(-60, -37.3) * mm, "mid": v(-57.87, -43.47) * mm, "end": v(-52.38, -47.01) * mm});
            skArc(sketch, "E79.16", {"start": v(-52.38, -47.01) * mm, "mid": v(0, -53.33) * mm, "end": v(52.38, -47.01) * mm});
            skArc(sketch, "E79.17", {"start": v(52.38, -47.01) * mm, "mid": v(57.87, -43.47) * mm, "end": v(60, -37.3) * mm});
            skLineSegment(sketch, "E79.18", {"start": v(60, 37.3) * mm, "end": v(60, -37.3) * mm});
            skArc(sketch, "E79.19", {"start": v(60, 37.3) * mm, "mid": v(57.87, 43.47) * mm, "end": v(52.38, 47.01) * mm});
            skLineSegment(sketch, "E80", {"start": v(0, 80) * mm, "end": v(0, 110) * mm, "construction": true});
            skPoint(sketch, "E80.endSnap0", {"position": v(0, 80) * mm});
            skCircle(sketch, "E81", {"center": v(0, 110) * mm, "radius": 6 * mm});
            skLineSegment(sketch, "E82", {"start": v(-30.68, 80) * mm, "end": v(-14.83, 98) * mm});
            skLineSegment(sketch, "E83", {"start": v(-14.83, 98) * mm, "end": v(-14.83, 104.33) * mm});
            skLineSegment(sketch, "E84", {"start": v(33.17, 80) * mm, "end": v(15.17, 98) * mm});
            skLineSegment(sketch, "E85", {"start": v(15.17, 98) * mm, "end": v(15.17, 104.33) * mm});
            skArc(sketch, "E86", {"start": v(15.17, 104.33) * mm, "mid": v(0.17, 119.33) * mm, "end": v(-14.83, 104.33) * mm});
            skLineSegment(sketch, "E87", {"start": v(-90, 0) * mm, "end": v(90, 0) * mm, "construction": true});
            skLineSegment(sketch, "E88.MirrorCS", {"start": v(33.17, -80) * mm, "end": v(15.17, -98) * mm});
            skLineSegment(sketch, "E89.MirrorCS", {"start": v(15.17, -98) * mm, "end": v(15.17, -104.33) * mm});
            skArc(sketch, "E90.MirrorCS", {"start": v(15.17, -104.33) * mm, "mid": v(0.17, -119.33) * mm, "end": v(-14.83, -104.33) * mm});
            skLineSegment(sketch, "E91.MirrorCS", {"start": v(-30.68, -80) * mm, "end": v(-14.83, -98) * mm});
            skLineSegment(sketch, "E92.MirrorCS", {"start": v(-14.83, -98) * mm, "end": v(-14.83, -104.33) * mm});
            skLineSegment(sketch, "E93.MirrorCS", {"start": v(0, -80) * mm, "end": v(0, -110) * mm, "construction": true});
            skCircle(sketch, "E94.MirrorC", {"center": v(0, -110) * mm, "radius": 6 * mm});
            skSolve(sketch);
        }
        {
            var Q0;
            Q0=makeQuery(id+"F16.imprint","IMPRINT",FACE,{"disambiguationData":[TD([[makeQuery(id+"F16.imprint","IMPRINT",EDGE,{"derivedFrom":sQuery(id+"F16.wireOp",EDGE,"E81")}),-1.0]])]});
            var Q1;
            {var subQ9=sQuery(id+"F16.wireOp",EDGE,"E79.0");Q1=makeQuery(id+"F16.imprint","IMPRINT",FACE,{"disambiguationData":[TD([[makeQuery(id+"F16.imprint","IMPRINT",EDGE,{"derivedFrom":subQ9}),1.0]])]});}
            var Q2;
            {var subQ0=sQuery(id+"F16.wireOp",EDGE,"E88.MirrorCS");Q2=makeQuery(id+"F16.imprint","IMPRINT",FACE,{"disambiguationData":[TD([[makeQuery(id+"F16.imprint","IMPRINT",EDGE,{"derivedFrom":subQ0}),-1.0]])]});}
            extrude(context, id + "F17", {"entities" : qUnion([Q0, Q1, Q2]), "operationType" : NewBodyOperationType.ADD, "endBound" : BoundingType.SYMMETRIC, "depth" : 6 * mm});
        }
    });
